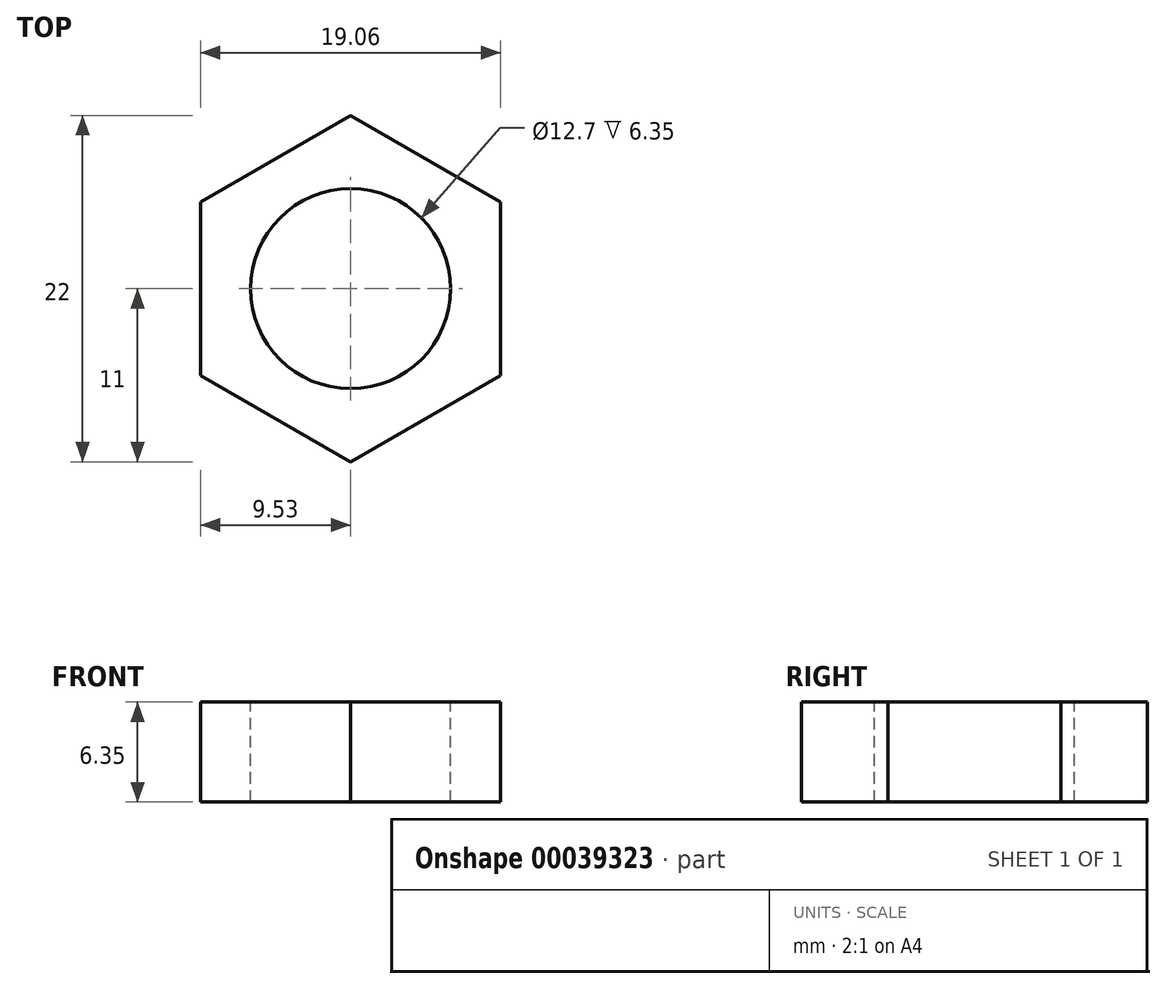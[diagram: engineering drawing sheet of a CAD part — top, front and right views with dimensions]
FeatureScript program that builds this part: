
annotation { "Feature Type Name" : "Feature", "Feature Type Description" : "" }
export const myFeature = defineFeature(function(context is Context, id is Id, definition is map)
    precondition{}
    {
        {
            var Q0;
            Q0=qCreatedBy(makeId("Top.planeOp"),FACE);
            var sketch = newSketch(context, id + "F0", { "sketchPlane" : qUnion([Q0])});
            skCircle(sketch, "E0.cCircle", {"center": v(0, 0) * mm, "radius": 9.52 * mm, "construction": true});
            skLineSegment(sketch, "E0.0", {"start": v(9.53, 5.5) * mm, "end": v(9.53, -5.5) * mm});
            skLineSegment(sketch, "E0.1", {"start": v(9.53, -5.5) * mm, "end": v(0, -11) * mm});
            skLineSegment(sketch, "E0.2", {"start": v(0, -11) * mm, "end": v(-9.53, -5.5) * mm});
            skLineSegment(sketch, "E0.3", {"start": v(-9.52, -5.5) * mm, "end": v(-9.52, 5.5) * mm});
            skLineSegment(sketch, "E0.4", {"start": v(-9.52, 5.5) * mm, "end": v(0, 11) * mm});
            skLineSegment(sketch, "E0.5", {"start": v(0, 11) * mm, "end": v(9.53, 5.5) * mm});
            skPoint(sketch, "E0.0.midPoint", {"position": v(9.52, 0) * mm});
            skCircle(sketch, "E1", {"center": v(0, 0) * mm, "radius": 6.35 * mm});
            skSolve(sketch);
        }
        {
            var Q0;
            Q0 = qSketchRegion(id + "F0", true);
            extrude(context, id + "F1", {"entities" : qUnion([Q0]), "oppositeDirection" : true, "depth" : 6.35 * mm});
        }
    });
